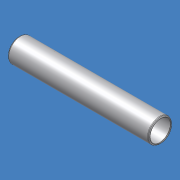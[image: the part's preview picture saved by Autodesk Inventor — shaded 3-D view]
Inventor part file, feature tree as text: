
AUTODESK INVENTOR PART (.ipt)
format: ipt  version: 2012 (Build 160160000, 160)  size: 112,128 bytes
history: native  units: mm (DEFAULTED — no unit token found)
features: other x42, revolve x1, sketch x1
ambient origin geometry x8: Origin, YZ Plane, XZ Plane, XY Plane, X Axis, Y Axis, Z Axis, Center Point
bodies: Solid1 (feature_tree)
feature tree (44):
  revolve  "Revolution1"  [1 undecoded]
  other  "tube_front_XY"
  other  "tube_front_YZ"
  other  "tube_front_ZX"
  other  "tube_front_X"
  other  "tube_front_Y"
  other  "tube_front_Z"
  other  "tube_front_Center"
  other  "tube_rear_XY"
  other  "tube_rear_YZ"
  other  "tube_rear_ZX"
  other  "tube_rear_X"
  other  "tube_rear_Y"
  other  "tube_rear_Z"
  other  "tube_rear_Center"
  other  "cp1_XY"
  other  "cp1_YZ"
  other  "cp1_ZX"
  other  "cp1_X"
  other  "cp1_Y"
  other  "cp1_Z"
  other  "cp1_Center"
  other  "cp2_XY"
  other  "cp2_YZ"
  other  "cp2_ZX"
  other  "cp2_X"
  other  "cp2_Y"
  other  "cp2_Z"
  other  "cp2_Center"
  other  "cp3_XY"
  other  "cp3_YZ"
  other  "cp3_ZX"
  other  "cp3_X"
  other  "cp3_Y"
  other  "cp3_Z"
  other  "cp3_Center"
  other  "cp4_XY"
  other  "cp4_YZ"
  other  "cp4_ZX"
  other  "cp4_X"
  other  "cp4_Y"
  other  "cp4_Z"
  other  "cp4_Center"
  sketch  "Sketch_1"  dims[d0=360.0deg]
note: 1 required parameter value undecoded (feature->parameter linkage not recoverable at this tier; creation-order binding heuristic only, values carry confidence <= 0.55)
